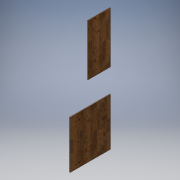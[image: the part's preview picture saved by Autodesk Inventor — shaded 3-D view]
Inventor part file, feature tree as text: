
AUTODESK INVENTOR PART (.ipt)
format: ipt  version: 2016 (Build 200138000, 138)  size: 128,000 bytes
history: native  units: mm
features: extrude x1, sketch x1
ambient origin geometry x8: Origin, YZ Plane, XZ Plane, XY Plane, X Axis, Y Axis, Z Axis, Center Point
bodies: Solid1 (feature_tree)
feature tree (2):
  extrude  "Extrusion1"  Depth=10.0mm
  sketch  "Sketch1"  dims[d0=80.0mm d7=10.0mm d8=0.0mm]
